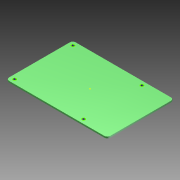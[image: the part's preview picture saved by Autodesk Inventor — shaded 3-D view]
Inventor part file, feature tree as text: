
AUTODESK INVENTOR PART (.ipt)
format: ipt  version: 2016 (Build 200138000, 138)  size: 95,744 bytes
history: native  units: in
note: dims shown in document units (in); Inventor stores cm internally (conversion verified against a paired STEP export)
features: other x2, sketch x1, imported_body x1
ambient origin geometry x8: Origin, YZ Plane, XZ Plane, XY Plane, X Axis, Y Axis, Z Axis, Center Point
bodies: Body1 (feature_tree)
feature tree (4):
  other  "Estrusione-Estrusione1"
  other  "Mainboard2.ipt1"
  sketch  "Sketch1"
  imported_body  "Base1"
